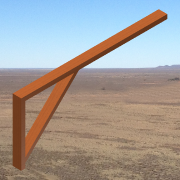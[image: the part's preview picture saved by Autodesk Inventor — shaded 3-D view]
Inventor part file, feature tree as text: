
AUTODESK INVENTOR PART (.ipt)
format: ipt  version: 2014 SP1 (Build 180222100, 222)  size: 155,648 bytes
history: native  units: in
note: dims shown in document units (in); Inventor stores cm internally (conversion verified against a paired STEP export)
features: sketch x4, extrude x2, loft x1
ambient origin geometry x8: Origin, YZ Plane, XZ Plane, XY Plane, X Axis, Y Axis, Z Axis, Center Point
bodies: Solid1 (feature_tree)
feature tree (7):
  extrude  "Extrusion1"  Depth=1.75in
  extrude  "Extrusion2"  Depth=1.75in
  loft  "Loft2"
  sketch  "Sketch1"  dims[d0=3.5in d1=1.75in]
  sketch  "Sketch2"  dims[d2=60.0in d3=0.0in d4=1.75in]
  sketch  "Sketch5"  dims[d5=24.0in d6=0.0in d12=20.0in]
  sketch  "Sketch6"  dims[d13=2.0in d14=20.0in d15=2.0in d16=0.0in d17=90.0deg d18=0.0in d19=90.0deg]
